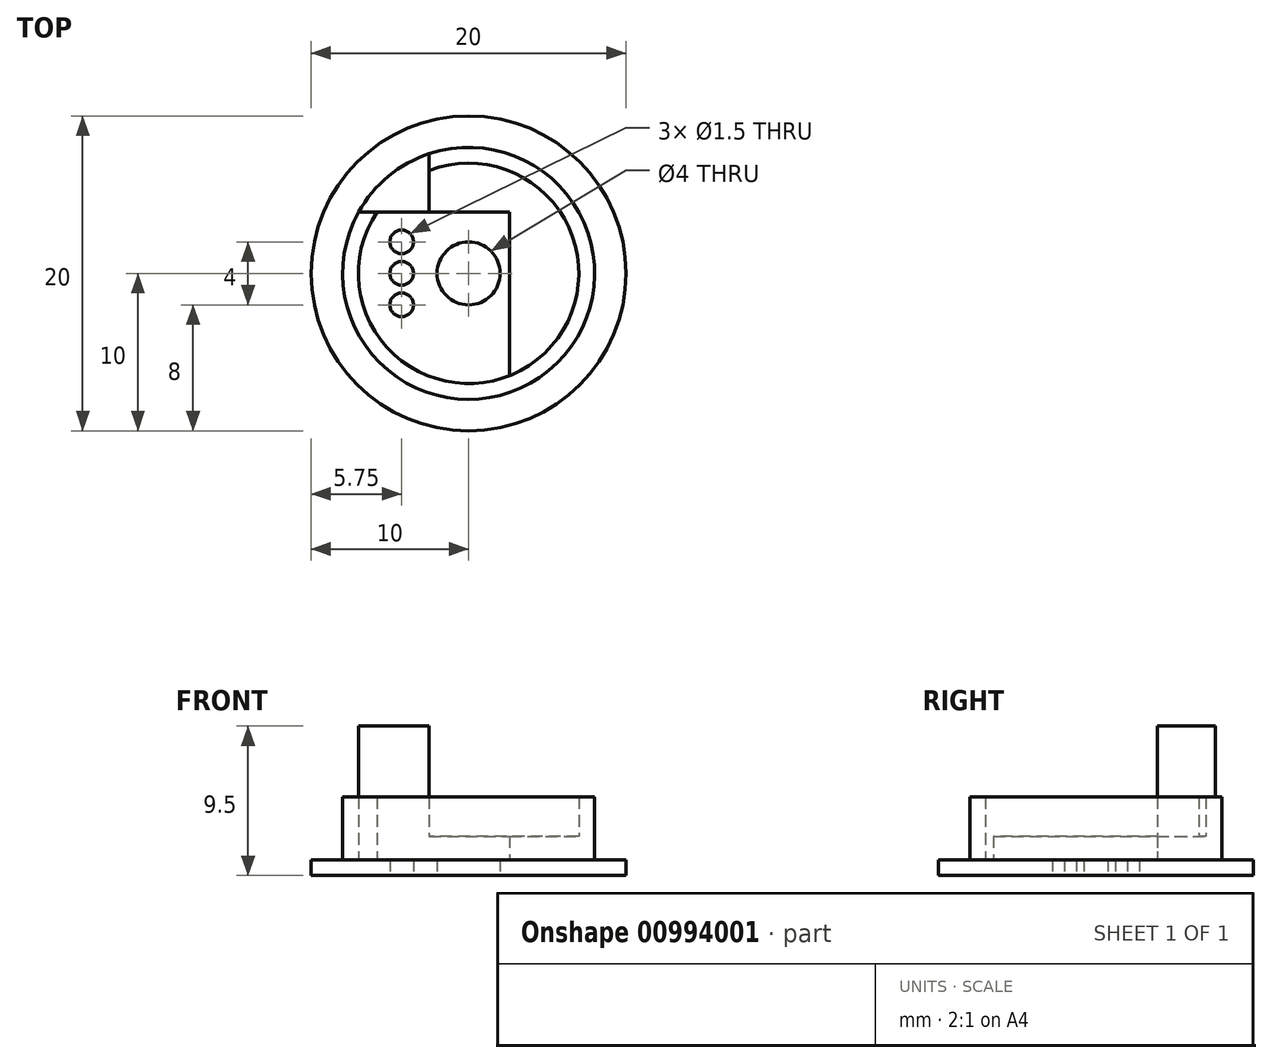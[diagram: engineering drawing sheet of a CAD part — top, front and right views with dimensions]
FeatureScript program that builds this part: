
annotation { "Feature Type Name" : "Feature", "Feature Type Description" : "" }
export const myFeature = defineFeature(function(context is Context, id is Id, definition is map)
    precondition{}
    {
        {
            var Q0;
            Q0=qCreatedBy(makeId("Top.planeOp"),FACE);
            var sketch = newSketch(context, id + "F0", { "sketchPlane" : qUnion([Q0])});
            skCircle(sketch, "E0", {"center": v(0, 0) * mm, "radius": 10 * mm});
            skCircle(sketch, "E1", {"center": v(0, 0) * mm, "radius": 8 * mm});
            skCircle(sketch, "E2", {"center": v(0, 0) * mm, "radius": 7 * mm});
            skCircle(sketch, "E3", {"center": v(0, 0) * mm, "radius": 2 * mm});
            skSolve(sketch);
        }
        {
            var Q0;
            Q0=makeQuery(id+"F0.imprint","IMPRINT",FACE,{"disambiguationData":[TD([[makeQuery(id+"F0.imprint","IMPRINT",EDGE,{"derivedFrom":sQuery(id+"F0.wireOp",EDGE,"E0")}),1.0]])]});
            var Q1;
            Q1=makeQuery(id+"F0.imprint","IMPRINT",FACE,{"disambiguationData":[TD([[makeQuery(id+"F0.imprint","IMPRINT",EDGE,{"derivedFrom":sQuery(id+"F0.wireOp",EDGE,"E1")}),1.0]])]});
            var Q2;
            Q2=makeQuery(id+"F0.imprint","IMPRINT",FACE,{"disambiguationData":[TD([[makeQuery(id+"F0.imprint","IMPRINT",EDGE,{"derivedFrom":sQuery(id+"F0.wireOp",EDGE,"E2")}),1.0]])]});
            extrude(context, id + "F1", {"entities" : qUnion([Q0, Q1, Q2]), "depth" : 1 * mm, "offsetDistance" : 25 * mm});
        }
        {
            var Q0;
            Q0=makeQuery(id+"F0.imprint","IMPRINT",FACE,{"disambiguationData":[TD([[makeQuery(id+"F0.imprint","IMPRINT",EDGE,{"derivedFrom":sQuery(id+"F0.wireOp",EDGE,"E1")}),1.0]])]});
            extrude(context, id + "F2", {"entities" : qUnion([Q0]), "operationType" : NewBodyOperationType.ADD, "depth" : 5 * mm, "offsetDistance" : 25 * mm});
        }
        {
            var Q0;
            {var subQ0=sQuery(id+"F0.wireOp",EDGE,"E3");Q0=makeQuery(id+"F2.boolean.opBoolean","SPLIT",FACE,{"disambiguationData":[TD([makeQuery(id+"F1.opExtrude","SWEPT_FACE",FACE,{"disambiguationData":[OSD([subQ0])]})])],"derivedFrom":makeQuery(id+"F1.opExtrude","CAP_FACE",FACE,{"disambiguationData":[OSD([sQuery(id+"F0.wireOp",EDGE,"E0"),subQ0])],"isStart":false})});}
            var sketch = newSketch(context, id + "F3", { "sketchPlane" : qUnion([Q0])});
            skLineSegment(sketch, "E4", {"start": v(-5.81, 3.9) * mm, "end": v(5.81, 3.9) * mm});
            skLineSegment(sketch, "E5", {"start": v(2.6, 6.5) * mm, "end": v(2.6, -6.5) * mm});
            skSolve(sketch);
        }
        {
            var Q0;
            {var subQ0=sQuery(id+"F3.wireOp",EDGE,"E4");var subQ3=sQuery(id+"F3.wireOp",EDGE,"E5");var subQ4=makeQuery(id+"F3.imprint","INTERSECT",VERTEX,{"derivedFrom":[subQ0,subQ3]});Q0=makeQuery(id+"F3.imprint","IMPRINT",FACE,{"disambiguationData":[TD([[makeQuery(id+"F3.imprint","IMPRINT",EDGE,{"disambiguationData":[TD([[subQ4,1.0]])],"derivedFrom":subQ0}),1.0]])]});}
            var Q1;
            {var subQ0=sQuery(id+"F3.wireOp",EDGE,"E4");var subQ3=sQuery(id+"F3.wireOp",EDGE,"E5");var subQ4=makeQuery(id+"F3.imprint","INTERSECT",VERTEX,{"derivedFrom":[subQ0,subQ3]});Q1=makeQuery(id+"F3.imprint","IMPRINT",FACE,{"disambiguationData":[TD([[makeQuery(id+"F3.imprint","IMPRINT",EDGE,{"disambiguationData":[TD([[subQ4,-1.0]])],"derivedFrom":subQ0}),1.0]])]});}
            var Q2;
            {var subQ0=sQuery(id+"F3.wireOp",EDGE,"E4");var subQ3=sQuery(id+"F3.wireOp",EDGE,"E5");var subQ4=makeQuery(id+"F3.imprint","INTERSECT",VERTEX,{"derivedFrom":[subQ0,subQ3]});Q2=makeQuery(id+"F3.imprint","IMPRINT",FACE,{"disambiguationData":[TD([[makeQuery(id+"F3.imprint","IMPRINT",EDGE,{"disambiguationData":[TD([[subQ4,-1.0]])],"derivedFrom":subQ0}),-1.0]])]});}
            extrude(context, id + "F4", {"entities" : qUnion([Q0, Q1, Q2]), "operationType" : NewBodyOperationType.ADD, "depth" : 1.5 * mm, "offsetDistance" : 25 * mm});
        }
        {
            var Q0;
            Q0=qCreatedBy(makeId("Top.planeOp"),FACE);
            var sketch = newSketch(context, id + "F5", { "sketchPlane" : qUnion([Q0])});
            skLineSegment(sketch, "E6", {"start": v(0, 0) * mm, "end": v(-4.25, 0) * mm});
            skLineSegment(sketch, "E7", {"start": v(-4.25, 0) * mm, "end": v(-4.25, -2) * mm});
            skLineSegment(sketch, "E8", {"start": v(-4.25, 0) * mm, "end": v(-4.25, 2) * mm});
            skCircle(sketch, "E9", {"center": v(-4.25, 2) * mm, "radius": 0.75 * mm});
            skCircle(sketch, "E10", {"center": v(-4.25, 0) * mm, "radius": 0.75 * mm});
            skCircle(sketch, "E11", {"center": v(-4.25, -2) * mm, "radius": 0.75 * mm});
            skSolve(sketch);
        }
        {
            var Q0;
            Q0=makeQuery(id+"F5.imprint","IMPRINT",FACE,{"disambiguationData":[TD([[makeQuery(id+"F5.imprint","IMPRINT",EDGE,{"derivedFrom":sQuery(id+"F5.wireOp",EDGE,"E9")}),1.0]])]});
            var Q1;
            {var subQ1=sQuery(id+"F5.wireOp",EDGE,"E6");var subQ3=sQuery(id+"F5.wireOp",EDGE,"E10");var subQ4=makeQuery(id+"F5.imprint","INTERSECT",VERTEX,{"derivedFrom":[subQ1,subQ3]});Q1=makeQuery(id+"F5.imprint","IMPRINT",FACE,{"disambiguationData":[TD([[makeQuery(id+"F5.imprint","IMPRINT",EDGE,{"disambiguationData":[TD([[subQ4,-1.0]])],"derivedFrom":subQ3}),1.0]])]});}
            var Q2;
            {var subQ1=sQuery(id+"F5.wireOp",EDGE,"E7");var subQ3=sQuery(id+"F5.wireOp",EDGE,"E10");var subQ4=makeQuery(id+"F5.imprint","INTERSECT",VERTEX,{"derivedFrom":[subQ1,subQ3]});Q2=makeQuery(id+"F5.imprint","IMPRINT",FACE,{"disambiguationData":[TD([[makeQuery(id+"F5.imprint","IMPRINT",EDGE,{"disambiguationData":[TD([[subQ4,1.0]])],"derivedFrom":subQ3}),1.0]])]});}
            var Q3;
            {var subQ1=sQuery(id+"F5.wireOp",EDGE,"E6");var subQ3=sQuery(id+"F5.wireOp",EDGE,"E10");var subQ4=makeQuery(id+"F5.imprint","INTERSECT",VERTEX,{"derivedFrom":[subQ1,subQ3]});Q3=makeQuery(id+"F5.imprint","IMPRINT",FACE,{"disambiguationData":[TD([[makeQuery(id+"F5.imprint","IMPRINT",EDGE,{"disambiguationData":[TD([[subQ4,1.0]])],"derivedFrom":subQ3}),1.0]])]});}
            var Q4;
            Q4=makeQuery(id+"F5.imprint","IMPRINT",FACE,{"disambiguationData":[TD([[makeQuery(id+"F5.imprint","IMPRINT",EDGE,{"derivedFrom":sQuery(id+"F5.wireOp",EDGE,"E11")}),1.0]])]});
            var Q5;
            {var subQ0=sQuery(id+"F0.wireOp",EDGE,"E3");Q5=makeQuery(id+"F2.boolean.opBoolean","SPLIT",FACE,{"disambiguationData":[TD([makeQuery(id+"F1.opExtrude","SWEPT_FACE",FACE,{"disambiguationData":[OSD([subQ0])]})])],"derivedFrom":makeQuery(id+"F1.opExtrude","CAP_FACE",FACE,{"disambiguationData":[OSD([sQuery(id+"F0.wireOp",EDGE,"E0"),subQ0])],"isStart":false})});}
            extrude(context, id + "F6", {"entities" : qUnion([Q0, Q1, Q2, Q3, Q4]), "operationType" : NewBodyOperationType.REMOVE, "endBound" : BoundingType.UP_TO_SURFACE, "depth" : 2.36 * mm, "endBoundEntityFace" : qUnion([Q5]), "offsetDistance" : 25 * mm});
        }
        {
            var Q0;
            Q0=qCreatedBy(makeId("Top.planeOp"),FACE);
            var sketch = newSketch(context, id + "F7", { "sketchPlane" : qUnion([Q0])});
            skCircle(sketch, "E12", {"center": v(0, 0) * mm, "radius": 8 * mm});
            skLineSegment(sketch, "E13", {"start": v(-2.5, 7.6) * mm, "end": v(-2.5, -7.6) * mm});
            skLineSegment(sketch, "E14", {"start": v(6.98, 3.9) * mm, "end": v(-6.98, 3.9) * mm});
            skSolve(sketch);
        }
        {
            var Q0;
            {var subQ0=sQuery(id+"F7.wireOp",EDGE,"E13");var subQ1=sQuery(id+"F7.wireOp",EDGE,"E12");var subQ2=makeQuery(id+"F7.imprint","INTERSECT",VERTEX,{"disambiguationData":[OD(0.0)],"derivedFrom":[subQ1,subQ0]});Q0=makeQuery(id+"F7.imprint","IMPRINT",FACE,{"disambiguationData":[TD([[makeQuery(id+"F7.imprint","IMPRINT",EDGE,{"disambiguationData":[TD([[subQ2,-1.0]])],"derivedFrom":subQ1}),1.0]])]});}
            extrude(context, id + "F8", {"entities" : qUnion([Q0]), "operationType" : NewBodyOperationType.ADD, "depth" : 9.5 * mm, "offsetDistance" : 25 * mm});
        }
    });
